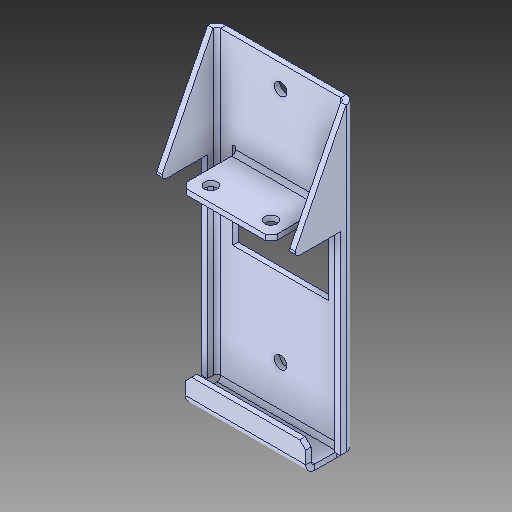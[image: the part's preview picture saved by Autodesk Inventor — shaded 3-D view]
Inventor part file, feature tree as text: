
AUTODESK INVENTOR PART (.ipt)
format: ipt  version: 2018 (Build 220112000, 112)  size: 154,624 bytes
history: native  units: in
note: dims shown in document units (in); Inventor stores cm internally (conversion verified against a paired STEP export)
features: chamfer x1
ambient origin geometry x8: Origin, YZ Plane, XZ Plane, XY Plane, X Axis, Y Axis, Z Axis, Center Point
bodies: Solid1 (feature_tree)
feature tree (1):
  chamfer  "Chamfer8"  [1 undecoded]
note: 1 required parameter value undecoded (feature->parameter linkage not recoverable at this tier; creation-order binding heuristic only, values carry confidence <= 0.55)
